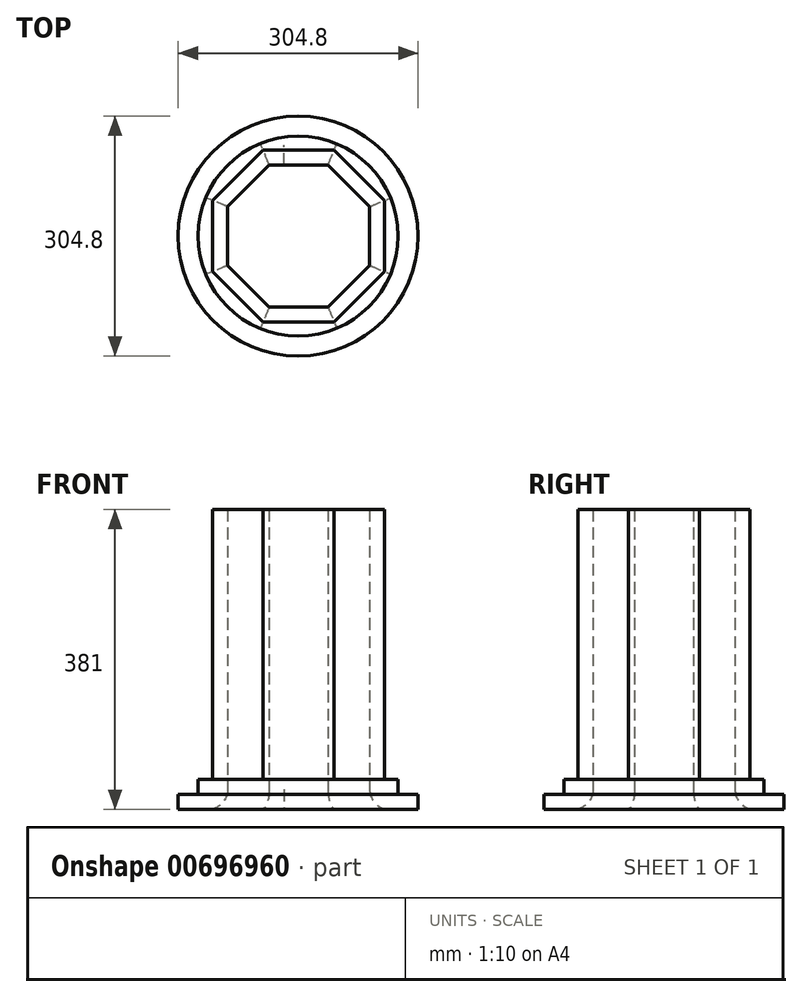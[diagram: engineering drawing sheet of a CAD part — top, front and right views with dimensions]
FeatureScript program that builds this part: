
annotation { "Feature Type Name" : "Feature", "Feature Type Description" : "" }
export const myFeature = defineFeature(function(context is Context, id is Id, definition is map)
    precondition{}
    {
        {
            var Q0;
            Q0=qCreatedBy(makeId("Top.planeOp"),FACE);
            var sketch = newSketch(context, id + "F0", { "sketchPlane" : qUnion([Q0])});
            skLineSegment(sketch, "E0.bottom", {"start": v(-36.69, 4.3) * mm, "end": v(-17.64, 4.3) * mm});
            skLineSegment(sketch, "E1", {"start": v(45.86, 23.34) * mm, "end": v(64.91, 4.3) * mm});
            skLineSegment(sketch, "E2", {"start": v(45.86, 23.34) * mm, "end": v(-17.64, 23.34) * mm});
            skLineSegment(sketch, "E3", {"start": v(-36.69, 4.3) * mm, "end": v(-89.48, -48.5) * mm});
            skLineSegment(sketch, "E4", {"start": v(-89.48, -21.55) * mm, "end": v(-44.58, 23.35) * mm});
            skLineSegment(sketch, "E5", {"start": v(-44.58, 23.35) * mm, "end": v(-17.64, 23.34) * mm});
            skLineSegment(sketch, "E6", {"start": v(-89.48, -48.5) * mm, "end": v(-89.48, -123.15) * mm});
            skLineSegment(sketch, "E7", {"start": v(-108.53, -104.1) * mm, "end": v(-108.53, -40.6) * mm});
            skLineSegment(sketch, "E8", {"start": v(-108.53, -40.6) * mm, "end": v(-89.48, -21.55) * mm});
            skLineSegment(sketch, "E9", {"start": v(-89.48, -123.15) * mm, "end": v(-36.7, -175.94) * mm});
            skLineSegment(sketch, "E10", {"start": v(-63.64, -175.94) * mm, "end": v(-108.54, -131.04) * mm});
            skLineSegment(sketch, "E11", {"start": v(-108.54, -131.04) * mm, "end": v(-108.53, -104.1) * mm});
            skLineSegment(sketch, "E12", {"start": v(-36.7, -175.94) * mm, "end": v(37.96, -175.94) * mm});
            skLineSegment(sketch, "E13", {"start": v(18.9, -195) * mm, "end": v(-44.6, -195) * mm});
            skLineSegment(sketch, "E14", {"start": v(-44.6, -195) * mm, "end": v(-63.64, -175.94) * mm});
            skLineSegment(sketch, "E15", {"start": v(37.96, -175.94) * mm, "end": v(90.74, -123.15) * mm});
            skLineSegment(sketch, "E16", {"start": v(18.9, -195) * mm, "end": v(45.85, -195) * mm});
            skLineSegment(sketch, "E17", {"start": v(45.85, -195) * mm, "end": v(90.75, -150.1) * mm});
            skLineSegment(sketch, "E18", {"start": v(90.75, -150.1) * mm, "end": v(109.8, -131.03) * mm});
            skLineSegment(sketch, "E19", {"start": v(109.8, -131.03) * mm, "end": v(109.8, -67.53) * mm});
            skLineSegment(sketch, "E20", {"start": v(90.75, -48.5) * mm, "end": v(37.94, 4.29) * mm});
            skLineSegment(sketch, "E21", {"start": v(64.91, 4.3) * mm, "end": v(109.81, -40.61) * mm});
            skLineSegment(sketch, "E22", {"start": v(109.81, -40.61) * mm, "end": v(109.8, -67.53) * mm});
            skLineSegment(sketch, "E23", {"start": v(90.75, -48.5) * mm, "end": v(90.74, -123.15) * mm});
            skLineSegment(sketch, "E24", {"start": v(-17.64, 4.3) * mm, "end": v(37.94, 4.29) * mm});
            skLineSegment(sketch, "E25", {"start": v(-89.48, -85.83) * mm, "end": v(90.75, -85.85) * mm});
            skCircle(sketch, "E26", {"center": v(0, -85.84) * mm, "radius": 127 * mm});
            skCircle(sketch, "E27", {"center": v(0, -85.84) * mm, "radius": 152.4 * mm});
            skSolve(sketch);
        }
        {
            var Q0;
            Q0=makeQuery(id+"F0.imprint","IMPRINT",FACE,{"disambiguationData":[TD([[makeQuery(id+"F0.imprint","IMPRINT",EDGE,{"derivedFrom":sQuery(id+"F0.wireOp",EDGE,"E0.bottom")}),1.0]])]});
            extrude(context, id + "F1", {"entities" : qUnion([Q0]), "depth" : 381 * mm, "offsetDistance" : 25.4 * mm});
        }
        {
            var Q0;
            Q0=makeQuery(id+"F0.imprint","IMPRINT",FACE,{"disambiguationData":[TD([[makeQuery(id+"F0.imprint","IMPRINT",EDGE,{"derivedFrom":sQuery(id+"F0.wireOp",EDGE,"E1")}),1.0]])]});
            extrude(context, id + "F2", {"entities" : qUnion([Q0]), "operationType" : NewBodyOperationType.ADD, "depth" : 38.1 * mm, "offsetDistance" : 25.4 * mm});
        }
        {
            var Q0;
            Q0=makeQuery(id+"F0.imprint","IMPRINT",FACE,{"disambiguationData":[TD([[makeQuery(id+"F0.imprint","IMPRINT",EDGE,{"derivedFrom":sQuery(id+"F0.wireOp",EDGE,"E26")}),-1.0]])]});
            extrude(context, id + "F3", {"entities" : qUnion([Q0]), "operationType" : NewBodyOperationType.ADD, "depth" : 19.05 * mm, "offsetDistance" : 25.4 * mm});
        }
        {
            var Q0;
            Q0=makeQuery(id+"F1.opExtrude","CAP_EDGE",EDGE,{"disambiguationData":[OSD([sQuery(id+"F0.wireOp",EDGE,"E6")])],"isStart":true});
            var Q1;
            Q1=makeQuery(id+"F1.opExtrude","CAP_EDGE",EDGE,{"disambiguationData":[OSD([sQuery(id+"F0.wireOp",EDGE,"E9")])],"isStart":true});
            var Q2;
            Q2=makeQuery(id+"F1.opExtrude","CAP_EDGE",EDGE,{"disambiguationData":[OSD([sQuery(id+"F0.wireOp",EDGE,"E3")])],"isStart":true});
            var Q3;
            Q3=makeQuery(id+"F1.opExtrude","CAP_EDGE",EDGE,{"disambiguationData":[OSD([sQuery(id+"F0.wireOp",EDGE,"E0.bottom")])],"isStart":true});
            var Q4;
            Q4=makeQuery(id+"F1.opExtrude","CAP_EDGE",EDGE,{"disambiguationData":[OSD([sQuery(id+"F0.wireOp",EDGE,"E24")])],"isStart":true});
            var Q5;
            Q5=makeQuery(id+"F1.opExtrude","CAP_EDGE",EDGE,{"disambiguationData":[OSD([sQuery(id+"F0.wireOp",EDGE,"E12")])],"isStart":true});
            var Q6;
            Q6=makeQuery(id+"F1.opExtrude","CAP_EDGE",EDGE,{"disambiguationData":[OSD([sQuery(id+"F0.wireOp",EDGE,"E15")])],"isStart":true});
            var Q7;
            Q7=makeQuery(id+"F1.opExtrude","CAP_EDGE",EDGE,{"disambiguationData":[OSD([sQuery(id+"F0.wireOp",EDGE,"E23")])],"isStart":true});
            var Q8;
            Q8=makeQuery(id+"F1.opExtrude","CAP_EDGE",EDGE,{"disambiguationData":[OSD([sQuery(id+"F0.wireOp",EDGE,"E20")])],"isStart":true});
            fillet(context, id + "F4", {"entities" : qUnion([Q0, Q1, Q2, Q3, Q4, Q5, Q6, Q7, Q8]), "radius" : 25.4 * mm, "tangentPropagation" : true, "allowEdgeOverflow" : false});
        }
    });
